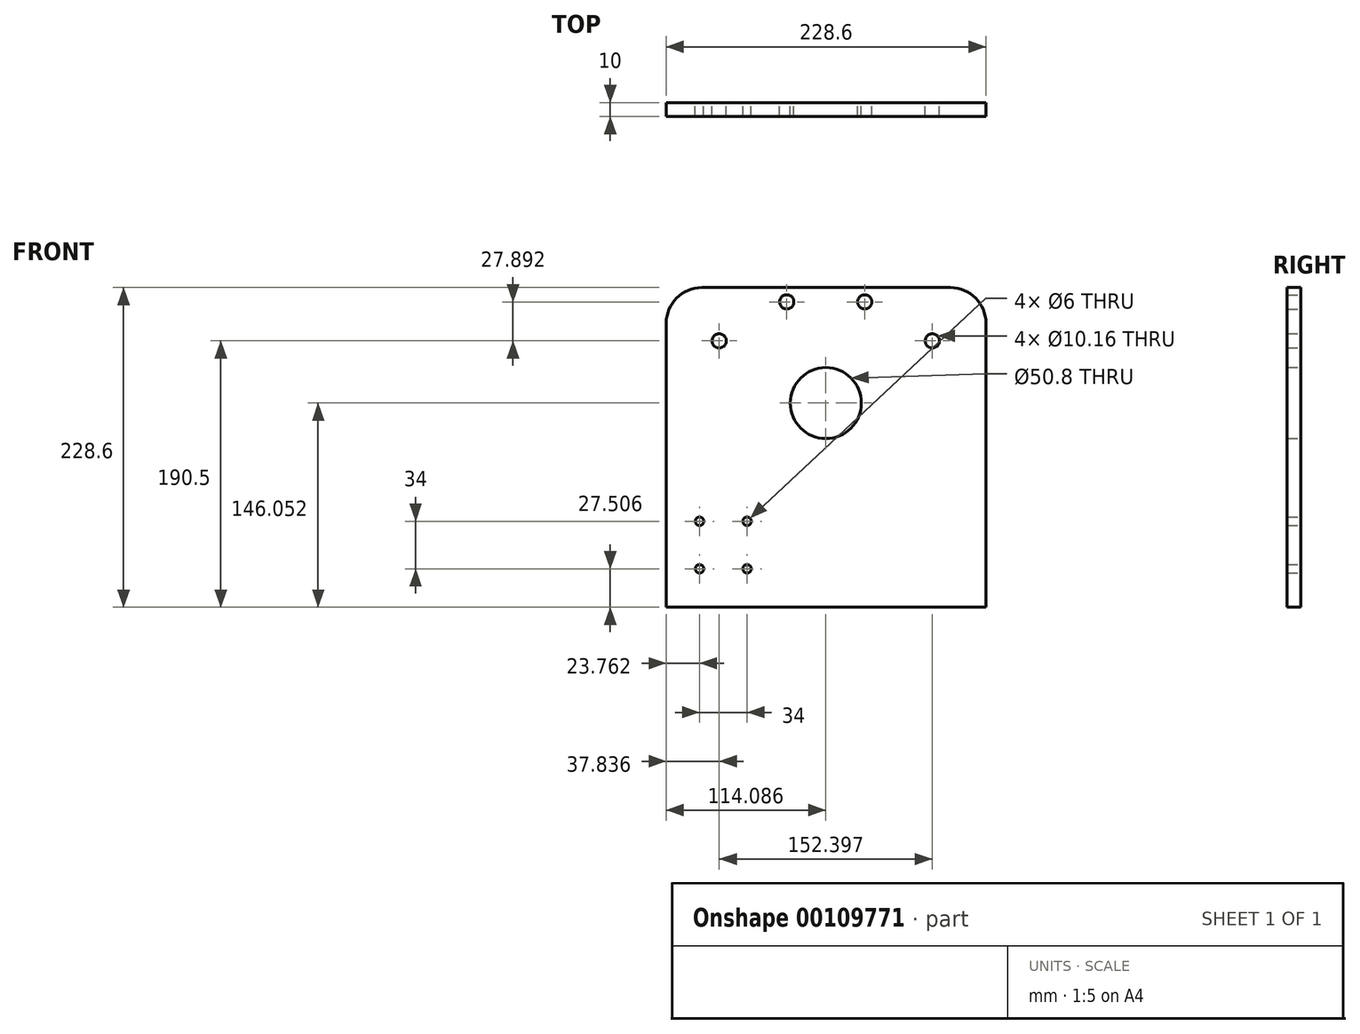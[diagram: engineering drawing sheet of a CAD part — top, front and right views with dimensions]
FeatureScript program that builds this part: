
annotation { "Feature Type Name" : "Feature", "Feature Type Description" : "" }
export const myFeature = defineFeature(function(context is Context, id is Id, definition is map)
    precondition{}
    {
        {
            var Q0;
            Q0=qCreatedBy(makeId("Front.planeOp"),FACE);
            var sketch = newSketch(context, id + "F0", { "sketchPlane" : qUnion([Q0])});
            skLineSegment(sketch, "E0.bottom", {"start": v(-114.3, -114.3) * mm, "end": v(114.3, -114.3) * mm});
            skLineSegment(sketch, "E0.top", {"start": v(-114.3, 114.3) * mm, "end": v(114.3, 114.3) * mm});
            skLineSegment(sketch, "E0.left", {"start": v(-114.3, -114.3) * mm, "end": v(-114.3, 114.3) * mm});
            skLineSegment(sketch, "E0.right", {"start": v(114.3, -114.3) * mm, "end": v(114.3, 114.3) * mm});
            skPoint(sketch, "E0.middle", {"position": v(0, 0) * mm});
            skCircle(sketch, "E1", {"center": v(-76.46, 76.2) * mm, "radius": 5.08 * mm});
            skLineSegment(sketch, "E2", {"start": v(0, 0) * mm, "end": v(-76.46, 76.2) * mm});
            skLineSegment(sketch, "E3", {"start": v(0, 0) * mm, "end": v(-114.3, 114.3) * mm, "construction": true});
            skCircle(sketch, "E4.1.0", {"center": v(-28.16, 104.1) * mm, "radius": 5.08 * mm});
            skCircle(sketch, "E4.2.0", {"center": v(27.62, 104.1) * mm, "radius": 5.08 * mm});
            skCircle(sketch, "E4.3.0", {"center": v(75.93, 76.2) * mm, "radius": 5.08 * mm});
            skPoint(sketch, "E4.center", {"position": v(-0.26, 0) * mm});
            skLineSegment(sketch, "E4.anchor1", {"start": v(-0.26, 0) * mm, "end": v(-76.46, 76.2) * mm, "construction": true});
            skLineSegment(sketch, "E4.anchor2", {"start": v(-0.26, 0) * mm, "end": v(75.93, 76.2) * mm, "construction": true});
            skLineSegment(sketch, "E5", {"start": v(0, 0) * mm, "end": v(-114.3, 0) * mm, "construction": true});
            skLineSegment(sketch, "E6", {"start": v(-76.46, 76.2) * mm, "end": v(-76.46, 0) * mm, "construction": true});
            skLineSegment(sketch, "E7", {"start": v(-76.46, 31.75) * mm, "end": v(76.04, 31.75) * mm, "construction": true});
            skLineSegment(sketch, "E8", {"start": v(75.93, 76.2) * mm, "end": v(76.04, 31.75) * mm, "construction": true});
            skCircle(sketch, "E9", {"center": v(-0.21, 31.75) * mm, "radius": 25.4 * mm});
            skLineSegment(sketch, "E10", {"start": v(-0.21, 31.75) * mm, "end": v(-0.26, 0) * mm, "construction": true});
            skCircle(sketch, "E11", {"center": v(-90.54, -86.8) * mm, "radius": 3 * mm});
            skCircle(sketch, "E12.0.1.0", {"center": v(-90.54, -52.8) * mm, "radius": 3 * mm});
            skCircle(sketch, "E12.1.0.0", {"center": v(-56.54, -86.8) * mm, "radius": 3 * mm});
            skCircle(sketch, "E12.1.1.0", {"center": v(-56.54, -52.8) * mm, "radius": 3 * mm});
            skLineSegment(sketch, "E12.direction1", {"start": v(-90.54, -86.8) * mm, "end": v(-56.54, -86.8) * mm, "construction": true});
            skLineSegment(sketch, "E12.direction2", {"start": v(-90.54, -86.8) * mm, "end": v(-90.54, -52.8) * mm, "construction": true});
            skSolve(sketch);
        }
        {
            var Q0;
            Q0=makeQuery(id+"F0.imprint","IMPRINT",FACE,{"disambiguationData":[TD([[makeQuery(id+"F0.imprint","IMPRINT",EDGE,{"derivedFrom":sQuery(id+"F0.wireOp",EDGE,"E0.bottom")}),1.0]])]});
            extrude(context, id + "F1", {"entities" : qUnion([Q0]), "depth" : 10 * mm, "offsetDistance" : 25.4 * mm});
        }
        {
            var Q0;
            Q0=makeQuery(id+"F1.opExtrude","SWEPT_EDGE",EDGE,{"disambiguationData":[OSD([sQuery(id+"F0.wireOp",EDGE,"E0.top"),sQuery(id+"F0.wireOp",EDGE,"E0.right")])]});
            var Q1;
            Q1=makeQuery(id+"F1.opExtrude","SWEPT_EDGE",EDGE,{"disambiguationData":[OSD([sQuery(id+"F0.wireOp",EDGE,"E0.top"),sQuery(id+"F0.wireOp",EDGE,"E0.left")])]});
            fillet(context, id + "F2", {"entities" : qUnion([Q0, Q1]), "radius" : 25.4 * mm, "tangentPropagation" : true, "allowEdgeOverflow" : false});
        }
    });
